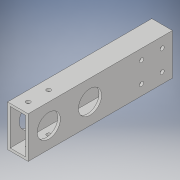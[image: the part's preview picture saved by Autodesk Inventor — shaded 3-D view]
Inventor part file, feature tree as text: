
AUTODESK INVENTOR PART (.ipt)
format: ipt  version: 2018 (Build 220112000, 112)  size: 164,864 bytes
history: native  units: in
note: dims shown in document units (in); Inventor stores cm internally (conversion verified against a paired STEP export)
features: extrude x2, hole x2, sketch x2, shell x1
ambient origin geometry x8: Origin, YZ Plane, XZ Plane, XY Plane, X Axis, Y Axis, Z Axis, Center Point
bodies: Solid1 (feature_tree)
feature tree (7):
  extrude  "Extrusion1"  Depth=7.0in
  shell  "Shell1"  Thickness=1.0in
  extrude  "Extrusion2"  Depth=1.0in
  hole  "Hole1"  [1 undecoded]
  hole  "Hole2"  [1 undecoded]
  sketch  "Sketch1"  dims[d0=2.0in d1=7.0in d2=1.0in d3=0.0in]
  sketch  "Sketch2"  dims[d4=0.125in d5=1.0in d6=1.125in d7=2.0in d8=1.125in d9=1.5in d10=1.5in d11=0.5in d12=0.5in d13=0.5in d14=0.5in d15=0.5in d16=0.5in d17=0.5in d18=0.5in d19=1.5in d20=1.5in d21=0.2031in d22=0.2031in d23=0.2031in d24=0.2031in d25=2.0in d26=0.0in d27=0.5in d28=0.5in d29=0.2031in d30=0.75in d31=0.375in d32=0.25in d33=0.5635in d34=1.0in d35=0.8108in d36=0.5in d37=1.5in d38=0.2031in d39=0.75in d40=0.375in d41=0.25in d42=0.5635in d43=1.0in d44=0.8108in]
note: 2 required parameter values undecoded (feature->parameter linkage not recoverable at this tier; creation-order binding heuristic only, values carry confidence <= 0.55)
